# Revit family: Shower-Bath_and_Shower_Trim-KOHLER-Archer-K-TS11078
name_source: partatom
category: Plumbing Fixtures
revit_build: Autodesk Revit 2017 (Build: 20160225_1515(x64)
units: mm (PartAtom-declared; Revit-internal decimal feet)

## family parameters
Cut with Voids When Loaded = No
Host = Face
OmniClass Number = 23.31.17.00
OmniClass Title = Showers
Part Type = Normal
Room Calculation Point = No
Round Connector Dimension = Use Diameter
Shared = No

## types (3) — shared parameters
ADA Compliant = No
Assembly Code = D2010700
CW Connection = No
Cold Water Inlet = Cold Water Inlet
Date Modified = 01/24/2020
Default Elevation = 42"
Drain Included = No
HW Connection = Yes
Handle Clearance = 3 1/4"
Height = 6 1/2"
Hot Water Inlet = Hot Water Inlet
Length = 6 1/2"
Manufacturer = KOHLER Co.
MasterFormat 1995 = 15410
MasterFormat 2004 = 22.41.23
Material = Premium Material Construction
Pressure = 80.00 psi
Product Documentation Link = https://www.us.kohler.com
Product Name = Archer
Product Page URL = http://www.us.kohler.com
Tempered Water Inlet = Tempered Water Inlet
URL = https://www.us.kohler.com
Vent Connection = No
Waste Connection = No
Waste Water Outlet = Waste Water Outlet
Width = 6 1/2"

## per-type parameters (varying)
| type | Description | Finish | Flow Rate | Model | Type | WaterSense Certified |
| 2.5 GPM,CP-Polished Chrome | Rite-Temp shower valve trim with lever handle and 2.5 gpm showerhead | Kohler-Metal-CP-Polished_Chrome | 3 GPM | K-TS11078-4-CP | 1 | No |
| 2.5 GPM,BN-Vibrant Brushed Nickel | Rite-Temp shower valve trim with lever handle and 2.5 gpm showerhead | Kohler-Metal-BN-Vibrant_Brushed_Nickel | 3 GPM | K-TS11078-4-BN | 2 | No |
| 2 GPM,CP-Polished Chrome | Rite-Temp shower trim set, valve not included | Kohler-Metal-CP-Polished_Chrome | 2 GPM | K-TS11078-4E-CP | 3 | Yes |

## geometry (parser evidence)
native form markers: Sweep x8
no freeform markers — native parametric forms only
